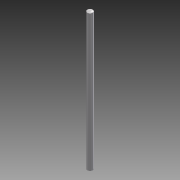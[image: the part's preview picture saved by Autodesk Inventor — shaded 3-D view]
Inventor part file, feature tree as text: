
AUTODESK INVENTOR PART (.ipt)
format: ipt  version: 2016 (Build 200138000, 138)  size: 87,040 bytes
history: native  units: mm
features: extrude x1, fillet x1, sketch x1
ambient origin geometry x8: Origin, YZ Plane, XZ Plane, XY Plane, X Axis, Y Axis, Z Axis, Center Point
bodies: Solid1 (feature_tree)
feature tree (3):
  extrude  "Extrusion1"  Depth=75.0mm TaperAngle=0.0deg
  fillet  "Fillet1"  Radius=0.1mm
  sketch  "Sketch1"  dims[d0=3.0mm d1=75.0mm d2=0.0mm d3=0.1mm]
